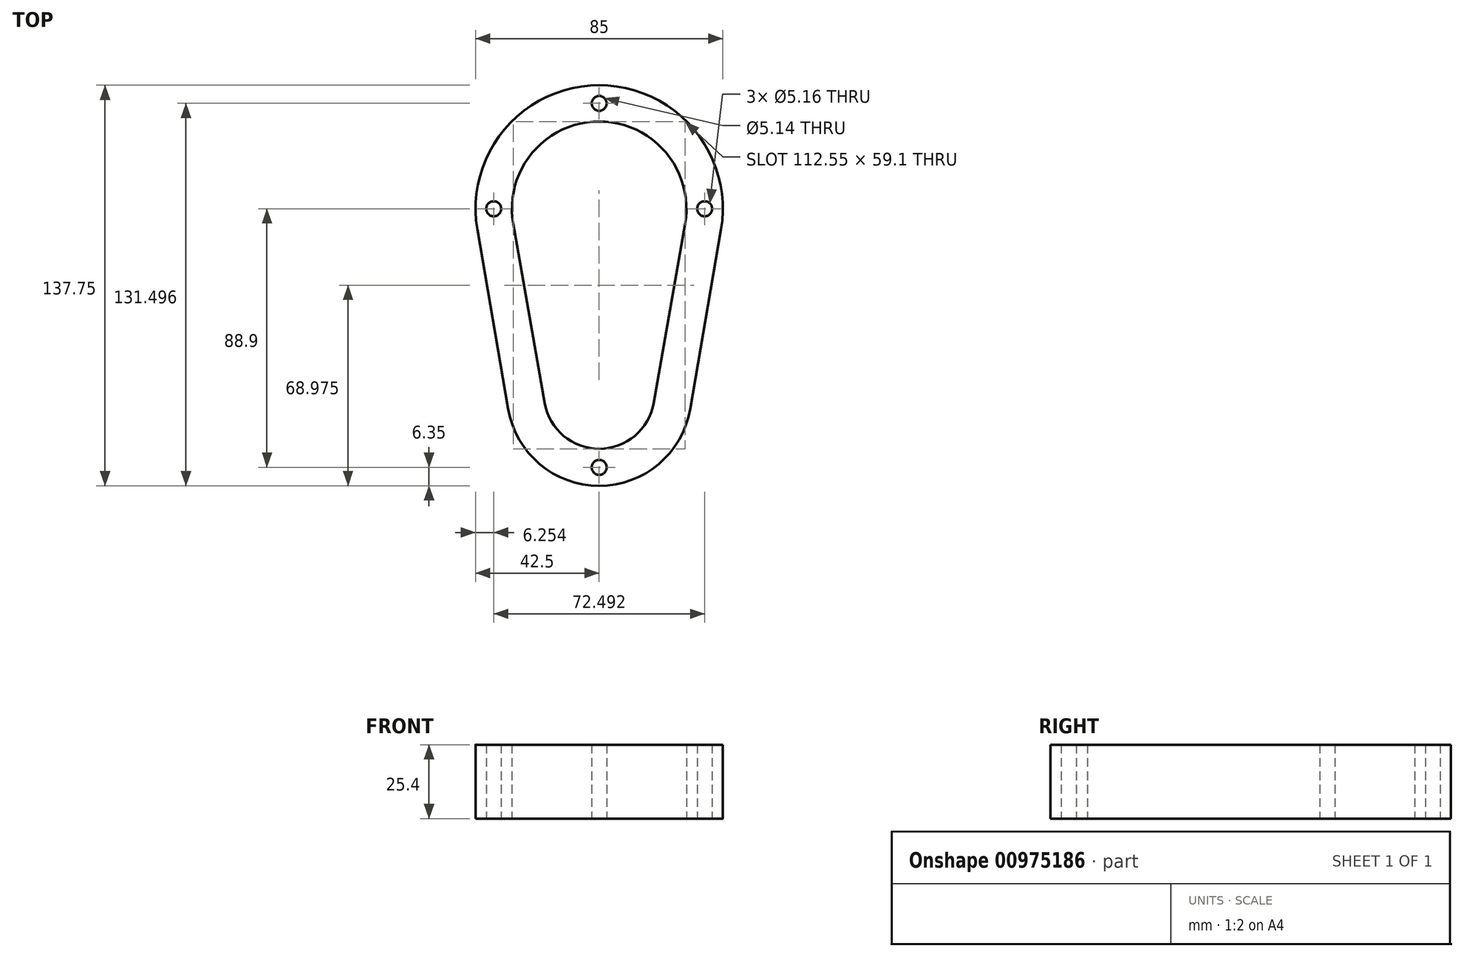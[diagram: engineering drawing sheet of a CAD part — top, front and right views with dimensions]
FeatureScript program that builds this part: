
annotation { "Feature Type Name" : "Feature", "Feature Type Description" : "" }
export const myFeature = defineFeature(function(context is Context, id is Id, definition is map)
    precondition{}
    {
        {
            var Q0;
            Q0=qCreatedBy(makeId("Top.planeOp"),FACE);
            var sketch = newSketch(context, id + "F0", { "sketchPlane" : qUnion([Q0])});
            skArc(sketch, "E0", {"start": v(29.55, -5.17) * mm, "mid": v(0, 30) * mm, "end": v(-29.55, -5.17) * mm});
            skArc(sketch, "E1", {"start": v(-18.76, -66.79) * mm, "mid": v(0, -82.55) * mm, "end": v(18.76, -66.79) * mm});
            skLineSegment(sketch, "E2", {"start": v(-41.89, -7.2) * mm, "end": v(-41.89, -7.2) * mm});
            skLineSegment(sketch, "E3", {"start": v(31.3, -68.88) * mm, "end": v(41.89, -7.2) * mm});
            skLineSegment(sketch, "E4", {"start": v(-41.89, -7.2) * mm, "end": v(-31.3, -68.88) * mm});
            skArc(sketch, "E5", {"start": v(41.89, -7.2) * mm, "mid": v(0, 42.5) * mm, "end": v(-41.89, -7.2) * mm});
            skArc(sketch, "E6", {"start": v(-41.89, -7.2) * mm, "mid": v(0, -42.5) * mm, "end": v(41.89, -7.2) * mm, "construction": true});
            skArc(sketch, "E7", {"start": v(31.3, -68.88) * mm, "mid": v(0, -31.75) * mm, "end": v(-31.3, -68.87) * mm, "construction": true});
            skArc(sketch, "E8", {"start": v(-31.3, -68.88) * mm, "mid": v(0, -95.25) * mm, "end": v(31.3, -68.88) * mm});
            skCircle(sketch, "E9", {"center": v(0, 0) * mm, "radius": 36.25 * mm, "construction": true});
            skCircle(sketch, "E10", {"center": v(0, 36.25) * mm, "radius": 2.57 * mm});
            skCircle(sketch, "E11", {"center": v(0, -88.9) * mm, "radius": 2.58 * mm});
            skCircle(sketch, "E12.1.0", {"center": v(-36.25, 0) * mm, "radius": 2.58 * mm});
            skCircle(sketch, "E12.2.0", {"center": v(0, -36.25) * mm, "radius": 2.58 * mm});
            skCircle(sketch, "E12.3.0", {"center": v(36.25, 0) * mm, "radius": 2.58 * mm});
            skLineSegment(sketch, "E13", {"start": v(-29.55, -5.17) * mm, "end": v(-18.76, -66.79) * mm});
            skLineSegment(sketch, "E14", {"start": v(18.76, -66.79) * mm, "end": v(29.55, -5.17) * mm});
            skSolve(sketch);
        }
        {
            var Q0;
            Q0=qSketchRegion(id+"F0",true);
            extrude(context, id + "F1", {"entities" : qUnion([Q0]), "depth" : 25.4 * mm, "offsetDistance" : 25.4 * mm});
        }
    });
